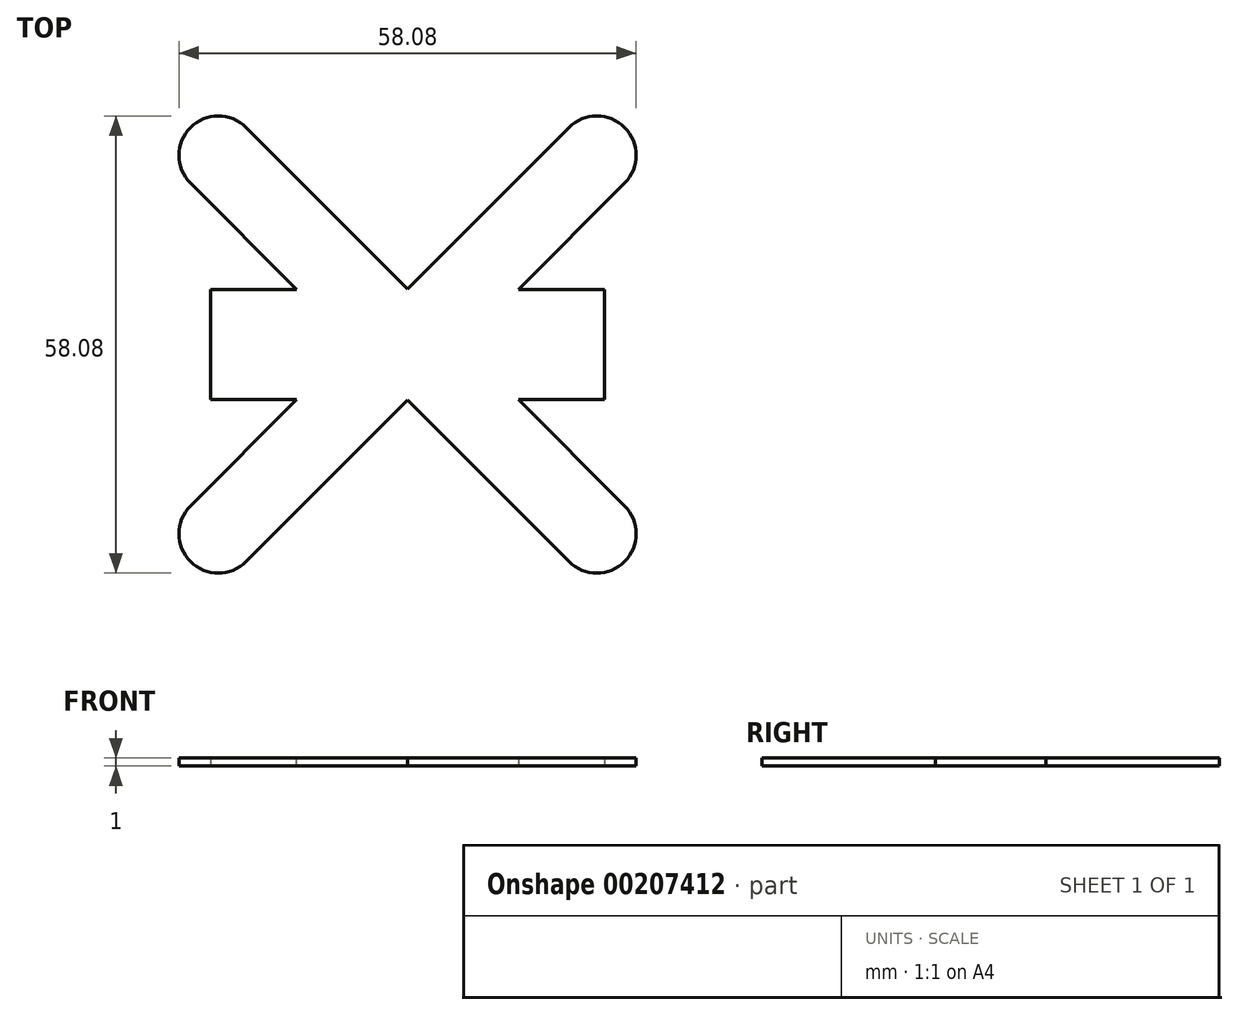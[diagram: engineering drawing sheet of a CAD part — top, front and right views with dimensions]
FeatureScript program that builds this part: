
annotation { "Feature Type Name" : "Feature", "Feature Type Description" : "" }
export const myFeature = defineFeature(function(context is Context, id is Id, definition is map)
    precondition{}
    {
        {
            var Q0;
            Q0=qCreatedBy(makeId("Front.planeOp"),FACE);
            var sketch = newSketch(context, id + "F0", { "sketchPlane" : qUnion([Q0])});
            skLineSegment(sketch, "E0", {"start": v(0, 0) * mm, "end": v(0, 31.85) * mm});
            skSolve(sketch);
        }
        {
            var Q0;
            Q0=qCreatedBy(makeId("Top.planeOp"),FACE);
            var sketch = newSketch(context, id + "F1", { "sketchPlane" : qUnion([Q0])});
            skLineSegment(sketch, "E1.bottom", {"start": v(5, -39) * mm, "end": v(-5, -39) * mm});
            skLineSegment(sketch, "E1.top", {"start": v(5, 39) * mm, "end": v(-5, 39) * mm});
            skLineSegment(sketch, "E1.left", {"start": v(5, -39) * mm, "end": v(5, 39) * mm});
            skLineSegment(sketch, "E1.right", {"start": v(-5, -39) * mm, "end": v(-5, 39) * mm});
            skPoint(sketch, "E1.middle", {"position": v(0, 0) * mm});
            skLineSegment(sketch, "E2.bottom", {"start": v(39, -5) * mm, "end": v(-39, -5) * mm});
            skLineSegment(sketch, "E2.top", {"start": v(39, 5) * mm, "end": v(-39, 5) * mm});
            skLineSegment(sketch, "E2.left", {"start": v(39, -5) * mm, "end": v(39, 5) * mm});
            skLineSegment(sketch, "E2.right", {"start": v(-39, -5) * mm, "end": v(-39, 5) * mm});
            skSolve(sketch);
        }
        {
            var Q0;
            Q0 = qSketchRegion(id + "F1", true);
            extrude(context, id + "F2", {"entities" : qUnion([Q0]), "depth" : 1 * mm});
        }
        {
            var Q0;
            Q0=makeQuery(id+"F2.opExtrude","SWEPT_BODY",BODY,{"disambiguationData":[OSD([sQuery(id+"F1.wireOp",EDGE,"E1.bottom"),sQuery(id+"F1.wireOp",EDGE,"E1.top"),sQuery(id+"F1.wireOp",EDGE,"E1.left"),sQuery(id+"F1.wireOp",EDGE,"E1.right"),sQuery(id+"F1.wireOp",EDGE,"E2.bottom"),sQuery(id+"F1.wireOp",EDGE,"E2.top"),sQuery(id+"F1.wireOp",EDGE,"E2.left"),sQuery(id+"F1.wireOp",EDGE,"E2.right")])]});
            var Q1;
            Q1=sQuery(id+"F0.wireOp",EDGE,"E0");
            transform(context, id + "F3", {"entities" : qUnion([Q0]), "transformType" : TransformType.ROTATION, "transformAxis" : qUnion([Q1]), "angle" : 45 * degree, "makeCopy" : false});
        }
        {
            var Q0;
            Q0=qCreatedBy(makeId("Top.planeOp"),FACE);
            var sketch = newSketch(context, id + "F4", { "sketchPlane" : qUnion([Q0])});
            skLineSegment(sketch, "E3.bottom", {"start": v(25, -7) * mm, "end": v(-25, -7) * mm});
            skLineSegment(sketch, "E3.top", {"start": v(25, 7) * mm, "end": v(-25, 7) * mm});
            skLineSegment(sketch, "E3.left", {"start": v(25, -7) * mm, "end": v(25, 7) * mm});
            skLineSegment(sketch, "E3.right", {"start": v(-25, -7) * mm, "end": v(-25, 7) * mm});
            skPoint(sketch, "E3.middle", {"position": v(0, 0) * mm});
            skSolve(sketch);
        }
        {
            var Q0;
            Q0 = qSketchRegion(id + "F4", true);
            extrude(context, id + "F5", {"entities" : qUnion([Q0]), "operationType" : NewBodyOperationType.ADD, "depth" : 1 * mm});
        }
        {
            var Q0;
            Q0=makeQuery(id+"F2.opExtrude","SWEPT_EDGE",EDGE,{"disambiguationData":[OSD([sQuery(id+"F1.wireOp",EDGE,"E1.top"),sQuery(id+"F1.wireOp",EDGE,"E1.right")])]});
            var Q1;
            Q1=makeQuery(id+"F2.opExtrude","SWEPT_EDGE",EDGE,{"disambiguationData":[OSD([sQuery(id+"F1.wireOp",EDGE,"E2.top"),sQuery(id+"F1.wireOp",EDGE,"E2.right")])]});
            var Q2;
            Q2=makeQuery(id+"F2.opExtrude","SWEPT_EDGE",EDGE,{"disambiguationData":[OSD([sQuery(id+"F1.wireOp",EDGE,"E2.bottom"),sQuery(id+"F1.wireOp",EDGE,"E2.right")])]});
            var Q3;
            Q3=makeQuery(id+"F2.opExtrude","SWEPT_EDGE",EDGE,{"disambiguationData":[OSD([sQuery(id+"F1.wireOp",EDGE,"E1.bottom"),sQuery(id+"F1.wireOp",EDGE,"E1.right")])]});
            var Q4;
            Q4=makeQuery(id+"F2.opExtrude","SWEPT_EDGE",EDGE,{"disambiguationData":[OSD([sQuery(id+"F1.wireOp",EDGE,"E2.bottom"),sQuery(id+"F1.wireOp",EDGE,"E2.left")])]});
            var Q5;
            Q5=makeQuery(id+"F2.opExtrude","SWEPT_EDGE",EDGE,{"disambiguationData":[OSD([sQuery(id+"F1.wireOp",EDGE,"E1.bottom"),sQuery(id+"F1.wireOp",EDGE,"E1.left")])]});
            var Q6;
            Q6=makeQuery(id+"F2.opExtrude","SWEPT_EDGE",EDGE,{"disambiguationData":[OSD([sQuery(id+"F1.wireOp",EDGE,"E2.top"),sQuery(id+"F1.wireOp",EDGE,"E2.left")])]});
            var Q7;
            Q7=makeQuery(id+"F2.opExtrude","SWEPT_EDGE",EDGE,{"disambiguationData":[OSD([sQuery(id+"F1.wireOp",EDGE,"E1.top"),sQuery(id+"F1.wireOp",EDGE,"E1.left")])]});
            fillet(context, id + "F6", {"entities" : qUnion([Q0, Q1, Q2, Q3, Q4, Q5, Q6, Q7]), "radius" : 5 * mm, "tangentPropagation" : true, "allowEdgeOverflow" : false});
        }
    });
